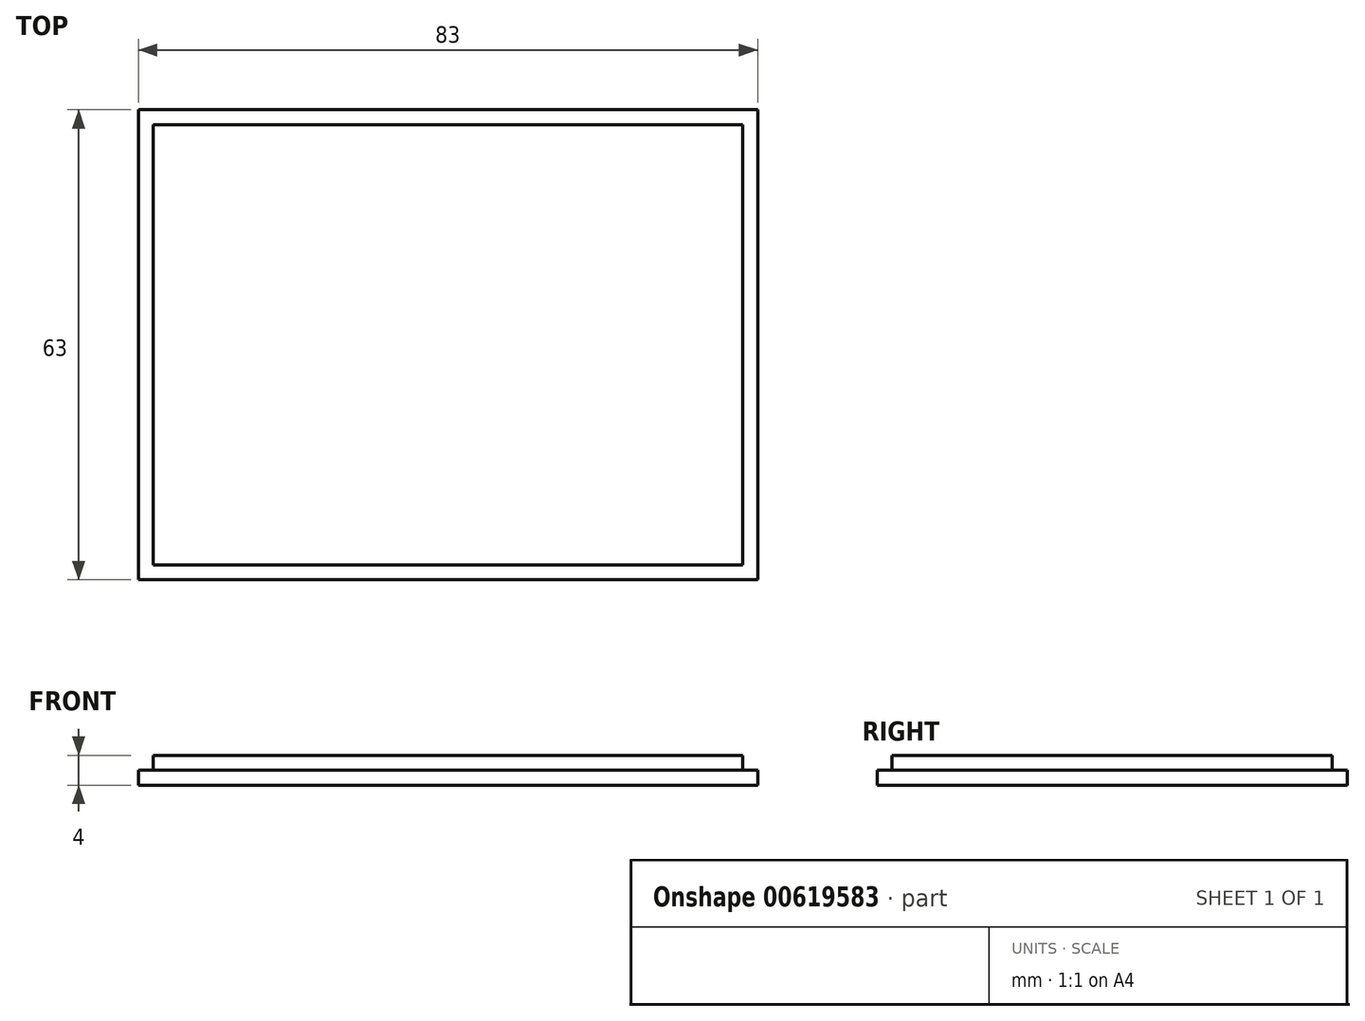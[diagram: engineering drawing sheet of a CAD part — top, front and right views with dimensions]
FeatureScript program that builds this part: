
annotation { "Feature Type Name" : "Feature", "Feature Type Description" : "" }
export const myFeature = defineFeature(function(context is Context, id is Id, definition is map)
    precondition{}
    {
        {
            var Q0;
            Q0=qCreatedBy(makeId("Top.planeOp"),FACE);
            var sketch = newSketch(context, id + "F0", { "sketchPlane" : qUnion([Q0])});
            skLineSegment(sketch, "E0.bottom", {"start": v(38.75, 28.5) * mm, "end": v(-36.25, 28.5) * mm});
            skLineSegment(sketch, "E0.top", {"start": v(38.75, -26.5) * mm, "end": v(-36.25, -26.5) * mm});
            skLineSegment(sketch, "E0.left", {"start": v(38.75, 28.5) * mm, "end": v(38.75, -26.5) * mm});
            skLineSegment(sketch, "E0.right", {"start": v(-36.25, 28.5) * mm, "end": v(-36.25, -26.5) * mm});
            skPoint(sketch, "E0.middle", {"position": v(1.25, 1) * mm});
            skLineSegment(sketch, "E1.0", {"start": v(42.75, 32.5) * mm, "end": v(-40.25, 32.5) * mm});
            skLineSegment(sketch, "E1.1", {"start": v(42.75, 32.5) * mm, "end": v(42.75, -30.5) * mm});
            skLineSegment(sketch, "E1.2", {"start": v(42.75, -30.5) * mm, "end": v(-40.25, -30.5) * mm});
            skLineSegment(sketch, "E1.3", {"start": v(-40.25, 32.5) * mm, "end": v(-40.25, -30.5) * mm});
            skLineSegment(sketch, "E2.0", {"start": v(40.75, 30.5) * mm, "end": v(-38.25, 30.5) * mm});
            skLineSegment(sketch, "E2.1", {"start": v(40.75, 30.5) * mm, "end": v(40.75, -28.5) * mm});
            skLineSegment(sketch, "E2.2", {"start": v(40.75, -28.5) * mm, "end": v(-38.25, -28.5) * mm});
            skLineSegment(sketch, "E2.3", {"start": v(-38.25, 30.5) * mm, "end": v(-38.25, -28.5) * mm});
            skSolve(sketch);
        }
        {
            var Q0;
            Q0=makeQuery(id+"F0.imprint","IMPRINT",FACE,{"disambiguationData":[TD([[makeQuery(id+"F0.imprint","IMPRINT",EDGE,{"derivedFrom":sQuery(id+"F0.wireOp",EDGE,"E0.bottom")}),1.0]])]});
            var Q1;
            Q1=makeQuery(id+"F0.imprint","IMPRINT",FACE,{"disambiguationData":[TD([[makeQuery(id+"F0.imprint","IMPRINT",EDGE,{"derivedFrom":sQuery(id+"F0.wireOp",EDGE,"E0.bottom")}),-1.0]])]});
            extrude(context, id + "F1", {"entities" : qUnion([Q0, Q1]), "depth" : 4 * mm, "offsetDistance" : 25 * mm});
        }
        {
            var Q0;
            Q0=makeQuery(id+"F0.imprint","IMPRINT",FACE,{"disambiguationData":[TD([[makeQuery(id+"F0.imprint","IMPRINT",EDGE,{"derivedFrom":sQuery(id+"F0.wireOp",EDGE,"E1.0")}),1.0]])]});
            extrude(context, id + "F2", {"entities" : qUnion([Q0]), "operationType" : NewBodyOperationType.ADD, "depth" : 2 * mm, "offsetDistance" : 25 * mm});
        }
    });
